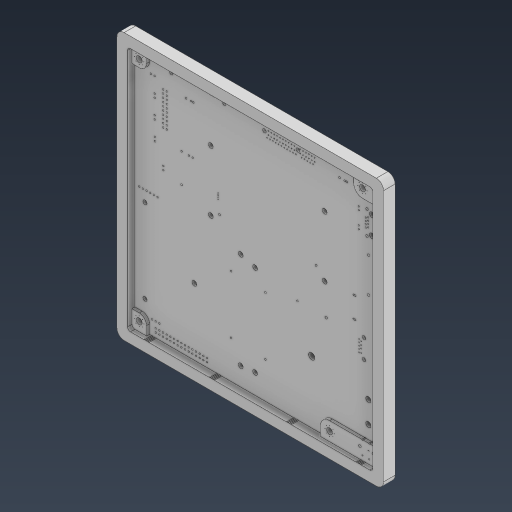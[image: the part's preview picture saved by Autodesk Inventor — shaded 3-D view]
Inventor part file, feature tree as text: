
AUTODESK INVENTOR PART (.ipt)
format: ipt  version: 2024.2 (Build 282272000, 272)  size: 767,488 bytes
history: native  units: mm
features: extrude x3, plane x1, sketch x1
ambient origin geometry x8: Origin, YZ Plane, XZ Plane, XY Plane, X Axis, Y Axis, Z Axis, Center Point
bodies: Body1 (feature_tree)
feature tree (5):
  plane  "工作平面1"
  sketch  "草圖1"
  extrude  "底板"  Depth=185.0mm
  extrude  "熱壓座"  Depth=185.0mm
  extrude  "擠出4"  Depth=5.0mm
